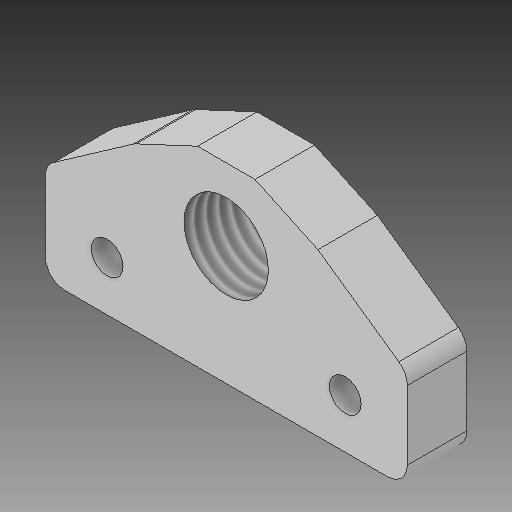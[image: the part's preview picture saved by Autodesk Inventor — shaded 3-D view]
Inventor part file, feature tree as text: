
AUTODESK INVENTOR PART (.ipt)
format: ipt  version: 2018 (Build 220112000, 112)  size: 133,120 bytes
history: native  units: mm
features: other x3, sketch x1
ambient origin geometry x8: Origin, YZ Plane, XZ Plane, XY Plane, X Axis, Y Axis, Z Axis, Center Point
bodies: Solid1 (feature_tree)
feature tree (4):
  other  "pshfit-mount-acrylic.ipt"
  other  "Solid1::pshfit-mount-acrylic.ipt"
  other  "TaggingFeature1"
  sketch  "Sketch1"  dims[d0=10.0mm]
